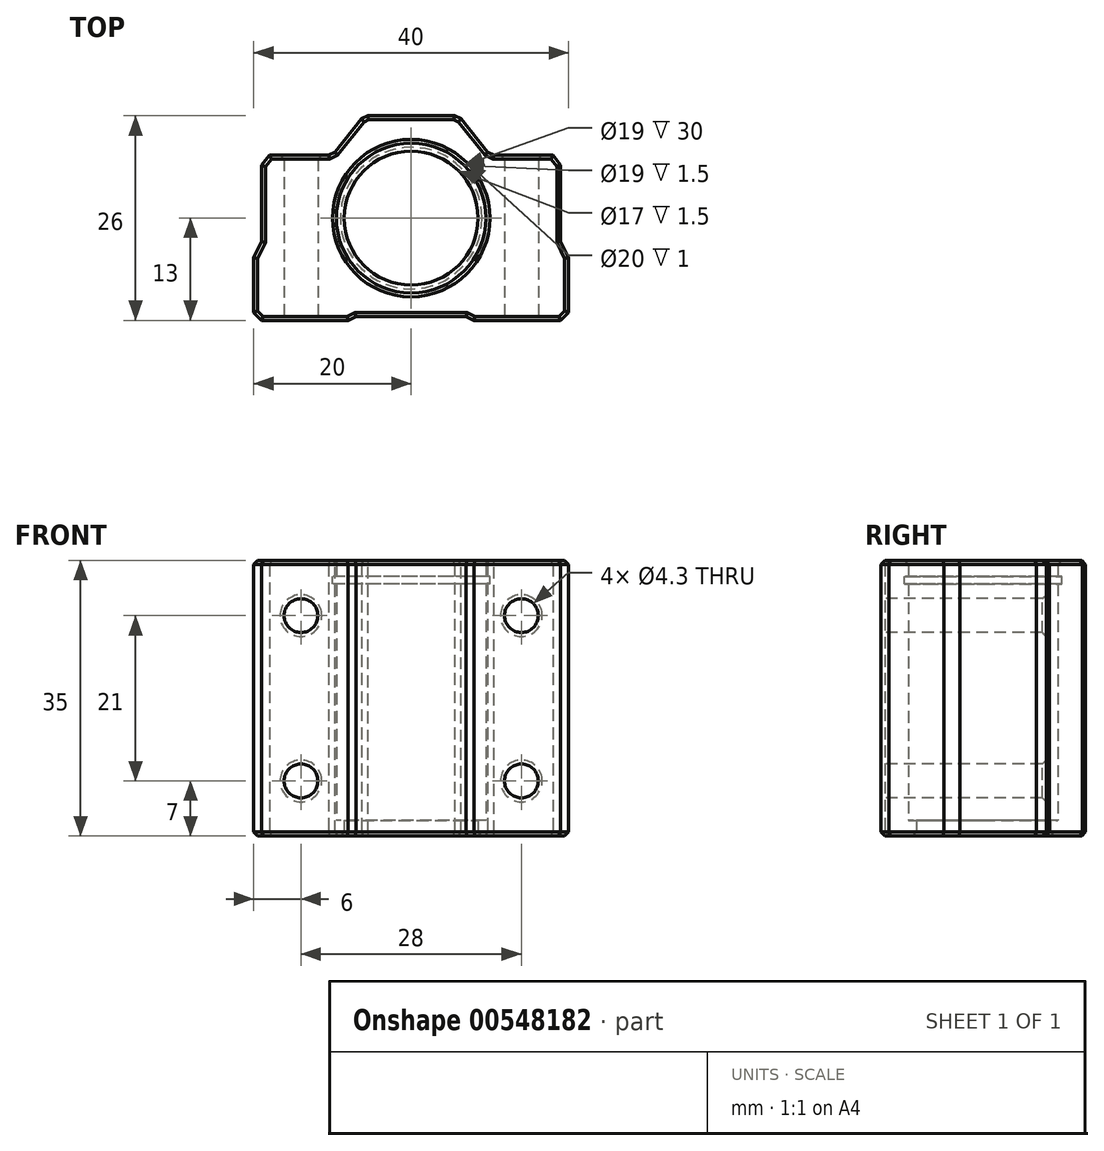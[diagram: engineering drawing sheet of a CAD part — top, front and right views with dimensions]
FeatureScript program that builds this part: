
annotation { "Feature Type Name" : "Feature", "Feature Type Description" : "" }
export const myFeature = defineFeature(function(context is Context, id is Id, definition is map)
    precondition{}
    {
        {
            var Q0;
            Q0=qCreatedBy(makeId("Top.planeOp"),FACE);
            var sketch = newSketch(context, id + "F0", { "sketchPlane" : qUnion([Q0])});
            skLineSegment(sketch, "E0", {"start": v(19, -13) * mm, "end": v(20, -12) * mm});
            skLineSegment(sketch, "E1", {"start": v(20, -12) * mm, "end": v(20, -5) * mm});
            skLineSegment(sketch, "E2", {"start": v(20, -5) * mm, "end": v(19, -3) * mm});
            skLineSegment(sketch, "E3", {"start": v(19, -3) * mm, "end": v(19, 6.72) * mm});
            skLineSegment(sketch, "E4", {"start": v(19, 6.72) * mm, "end": v(18, 8) * mm});
            skLineSegment(sketch, "E5", {"start": v(18, 8) * mm, "end": v(10, 8) * mm});
            skLineSegment(sketch, "E6", {"start": v(10, 8) * mm, "end": v(6, 13) * mm});
            skLineSegment(sketch, "E7", {"start": v(6, 13) * mm, "end": v(-6, 13) * mm});
            skLineSegment(sketch, "E8", {"start": v(-6, 13) * mm, "end": v(-10, 8) * mm});
            skLineSegment(sketch, "E9", {"start": v(-10, 8) * mm, "end": v(-18, 8) * mm});
            skLineSegment(sketch, "E10", {"start": v(-18, 8) * mm, "end": v(-19, 6.72) * mm});
            skLineSegment(sketch, "E11", {"start": v(-19, 6.72) * mm, "end": v(-19, -3) * mm});
            skLineSegment(sketch, "E12", {"start": v(-19, -3) * mm, "end": v(-20, -5) * mm});
            skLineSegment(sketch, "E13", {"start": v(-20, -5) * mm, "end": v(-20, -12) * mm});
            skLineSegment(sketch, "E14", {"start": v(-20, -12) * mm, "end": v(-19, -13) * mm});
            skCircle(sketch, "E15", {"center": v(0, 0) * mm, "radius": 9.5 * mm});
            skLineSegment(sketch, "E16", {"start": v(-19, -13) * mm, "end": v(-8, -13) * mm});
            skLineSegment(sketch, "E17", {"start": v(-8, -13) * mm, "end": v(-7, -12.5) * mm});
            skLineSegment(sketch, "E18", {"start": v(-7, -12.5) * mm, "end": v(7, -12.5) * mm});
            skLineSegment(sketch, "E19", {"start": v(7, -12.5) * mm, "end": v(8, -13) * mm});
            skLineSegment(sketch, "E20", {"start": v(8, -13) * mm, "end": v(19, -13) * mm});
            skSolve(sketch);
        }
        {
            var Q0;
            Q0=qSketchRegion(id+"F0",true);
            extrude(context, id + "F1", {"entities" : qUnion([Q0]), "depth" : 17.5 * mm, "offsetDistance" : 25 * mm, "hasSecondDirection" : true, "secondDirectionOppositeDirection" : true, "secondDirectionDepth" : 17.5 * mm});
        }
        {
            var Q0;
            Q0=makeQuery(id+"F1.opExtrude","SWEPT_FACE",FACE,{"disambiguationData":[OSD([sQuery(id+"F0.wireOp",EDGE,"E16")])]});
            var sketch = newSketch(context, id + "F2", { "sketchPlane" : qUnion([Q0])});
            skCircle(sketch, "E21", {"center": v(-14, 10.5) * mm, "radius": 2.15 * mm});
            skCircle(sketch, "E22", {"center": v(-14, -10.5) * mm, "radius": 2.15 * mm});
            skCircle(sketch, "E23", {"center": v(14, 10.5) * mm, "radius": 2.15 * mm});
            skCircle(sketch, "E24", {"center": v(14, -10.5) * mm, "radius": 2.15 * mm});
            skSolve(sketch);
        }
        {
            var Q0;
            Q0=makeQuery(id+"F2.imprint","IMPRINT",FACE,{"disambiguationData":[TD([[makeQuery(id+"F2.imprint","IMPRINT",EDGE,{"derivedFrom":sQuery(id+"F2.wireOp",EDGE,"E21")}),1.0]])]});
            var Q1;
            Q1=makeQuery(id+"F2.imprint","IMPRINT",FACE,{"disambiguationData":[TD([[makeQuery(id+"F2.imprint","IMPRINT",EDGE,{"derivedFrom":sQuery(id+"F2.wireOp",EDGE,"E23")}),1.0]])]});
            var Q2;
            Q2=makeQuery(id+"F2.imprint","IMPRINT",FACE,{"disambiguationData":[TD([[makeQuery(id+"F2.imprint","IMPRINT",EDGE,{"derivedFrom":sQuery(id+"F2.wireOp",EDGE,"E24")}),1.0]])]});
            var Q3;
            Q3=makeQuery(id+"F2.imprint","IMPRINT",FACE,{"disambiguationData":[TD([[makeQuery(id+"F2.imprint","IMPRINT",EDGE,{"derivedFrom":sQuery(id+"F2.wireOp",EDGE,"E22")}),1.0]])]});
            var Q4;
            Q4=sQuery(id+"F2.wireOp",EDGE,"E22");
            var Q5;
            Q5=sQuery(id+"F2.wireOp",EDGE,"E21");
            var Q6;
            Q6=sQuery(id+"F2.wireOp",EDGE,"E23");
            var Q7;
            Q7=sQuery(id+"F2.wireOp",EDGE,"E24");
            extrude(context, id + "F3", {"entities" : qUnion([Q0, Q1, Q2, Q3]), "operationType" : NewBodyOperationType.REMOVE, "surfaceEntities" : qUnion([Q4, Q5, Q6, Q7]), "oppositeDirection" : true, "depth" : 25 * mm, "offsetDistance" : 25 * mm});
        }
        {
            var Q0;
            Q0=makeQuery(id+"F3.boolean.opBoolean","INTERSECT",EDGE,{"derivedFrom":[makeQuery(id+"F1.opExtrude","SWEPT_FACE",FACE,{"disambiguationData":[OSD([sQuery(id+"F0.wireOp",EDGE,"E9")])]}),makeQuery(id+"F3.opExtrude","SWEPT_FACE",FACE,{"disambiguationData":[OSD([sQuery(id+"F2.wireOp",EDGE,"E21")])]})]});
            var Q1;
            Q1=makeQuery(id+"F3.boolean.opBoolean","INTERSECT",EDGE,{"derivedFrom":[makeQuery(id+"F1.opExtrude","SWEPT_FACE",FACE,{"disambiguationData":[OSD([sQuery(id+"F0.wireOp",EDGE,"E9")])]}),makeQuery(id+"F3.opExtrude","SWEPT_FACE",FACE,{"disambiguationData":[OSD([sQuery(id+"F2.wireOp",EDGE,"E22")])]})]});
            var Q2;
            Q2=makeQuery(id+"F3.boolean.opBoolean","INTERSECT",EDGE,{"derivedFrom":[makeQuery(id+"F1.opExtrude","SWEPT_FACE",FACE,{"disambiguationData":[OSD([sQuery(id+"F0.wireOp",EDGE,"E5")])]}),makeQuery(id+"F3.opExtrude","SWEPT_FACE",FACE,{"disambiguationData":[OSD([sQuery(id+"F2.wireOp",EDGE,"E24")])]})]});
            var Q3;
            Q3=makeQuery(id+"F3.boolean.opBoolean","INTERSECT",EDGE,{"derivedFrom":[makeQuery(id+"F1.opExtrude","SWEPT_FACE",FACE,{"disambiguationData":[OSD([sQuery(id+"F0.wireOp",EDGE,"E5")])]}),makeQuery(id+"F3.opExtrude","SWEPT_FACE",FACE,{"disambiguationData":[OSD([sQuery(id+"F2.wireOp",EDGE,"E23")])]})]});
            var Q4;
            Q4=makeQuery(id+"F3.boolean.opBoolean","COPY",EDGE,{"derivedFrom":makeQuery(id+"F3.opExtrude","CAP_EDGE",EDGE,{"disambiguationData":[OSD([sQuery(id+"F2.wireOp",EDGE,"E21")])],"isStart":true})});
            var Q5;
            Q5=makeQuery(id+"F3.boolean.opBoolean","COPY",EDGE,{"derivedFrom":makeQuery(id+"F3.opExtrude","CAP_EDGE",EDGE,{"disambiguationData":[OSD([sQuery(id+"F2.wireOp",EDGE,"E22")])],"isStart":true})});
            var Q6;
            Q6=makeQuery(id+"F3.boolean.opBoolean","COPY",EDGE,{"derivedFrom":makeQuery(id+"F3.opExtrude","CAP_EDGE",EDGE,{"disambiguationData":[OSD([sQuery(id+"F2.wireOp",EDGE,"E24")])],"isStart":true})});
            var Q7;
            Q7=makeQuery(id+"F3.boolean.opBoolean","COPY",EDGE,{"derivedFrom":makeQuery(id+"F3.opExtrude","CAP_EDGE",EDGE,{"disambiguationData":[OSD([sQuery(id+"F2.wireOp",EDGE,"E23")])],"isStart":true})});
            chamfer(context, id + "F4", {"entities" : qUnion([Q0, Q1, Q2, Q3, Q4, Q5, Q6, Q7]), "width" : .5 * mm, "tangentPropagation" : true});
        }
        {
            var Q0;
            Q0=makeQuery(id+"F1.opExtrude","CAP_FACE",FACE,{"disambiguationData":[OSD([sQuery(id+"F0.wireOp",EDGE,"E0"),sQuery(id+"F0.wireOp",EDGE,"E1"),sQuery(id+"F0.wireOp",EDGE,"E2"),sQuery(id+"F0.wireOp",EDGE,"E3"),sQuery(id+"F0.wireOp",EDGE,"E4"),sQuery(id+"F0.wireOp",EDGE,"E5"),sQuery(id+"F0.wireOp",EDGE,"E6"),sQuery(id+"F0.wireOp",EDGE,"E7"),sQuery(id+"F0.wireOp",EDGE,"E8"),sQuery(id+"F0.wireOp",EDGE,"E9"),sQuery(id+"F0.wireOp",EDGE,"E10"),sQuery(id+"F0.wireOp",EDGE,"E11"),sQuery(id+"F0.wireOp",EDGE,"E12"),sQuery(id+"F0.wireOp",EDGE,"E13"),sQuery(id+"F0.wireOp",EDGE,"E14"),sQuery(id+"F0.wireOp",EDGE,"E15"),sQuery(id+"F0.wireOp",EDGE,"E16"),sQuery(id+"F0.wireOp",EDGE,"E17"),sQuery(id+"F0.wireOp",EDGE,"E18"),sQuery(id+"F0.wireOp",EDGE,"E19"),sQuery(id+"F0.wireOp",EDGE,"E20")])],"isStart":true});
            var sketch = newSketch(context, id + "F5", { "sketchPlane" : qUnion([Q0])});
            skCircle(sketch, "E25", {"center": v(0, 0) * mm, "radius": 8.5 * mm});
            skSolve(sketch);
        }
        {
            var Q0;
            Q0=makeQuery(id+"F5.imprint","IMPRINT",FACE,{"disambiguationData":[TD([[makeQuery(id+"F5.imprint","IMPRINT",EDGE,{"derivedFrom":sQuery(id+"F5.wireOp",EDGE,"E25")}),-1.0]])]});
            extrude(context, id + "F6", {"entities" : qUnion([Q0]), "operationType" : NewBodyOperationType.ADD, "oppositeDirection" : true, "depth" : 2 * mm, "offsetDistance" : 25 * mm});
        }
        {
            var Q0;
            Q0=makeQuery(id+"F1.opExtrude","CAP_FACE",FACE,{"disambiguationData":[OSD([sQuery(id+"F0.wireOp",EDGE,"E0"),sQuery(id+"F0.wireOp",EDGE,"E1"),sQuery(id+"F0.wireOp",EDGE,"E2"),sQuery(id+"F0.wireOp",EDGE,"E3"),sQuery(id+"F0.wireOp",EDGE,"E4"),sQuery(id+"F0.wireOp",EDGE,"E5"),sQuery(id+"F0.wireOp",EDGE,"E6"),sQuery(id+"F0.wireOp",EDGE,"E7"),sQuery(id+"F0.wireOp",EDGE,"E8"),sQuery(id+"F0.wireOp",EDGE,"E9"),sQuery(id+"F0.wireOp",EDGE,"E10"),sQuery(id+"F0.wireOp",EDGE,"E11"),sQuery(id+"F0.wireOp",EDGE,"E12"),sQuery(id+"F0.wireOp",EDGE,"E13"),sQuery(id+"F0.wireOp",EDGE,"E14"),sQuery(id+"F0.wireOp",EDGE,"E15"),sQuery(id+"F0.wireOp",EDGE,"E16"),sQuery(id+"F0.wireOp",EDGE,"E17"),sQuery(id+"F0.wireOp",EDGE,"E18"),sQuery(id+"F0.wireOp",EDGE,"E19"),sQuery(id+"F0.wireOp",EDGE,"E20")])],"isStart":false});
            cPlane(context, id + "F7", {"entities" : qUnion([Q0]), "cplaneType" : CPlaneType.OFFSET, "offset" : 2 * mm, "oppositeDirection" : true, "width" : 150 * mm, "height" : 150 * mm});
        }
        {
            var Q0;
            Q0=qCreatedBy(id+"F7.planeOp",FACE);
            var sketch = newSketch(context, id + "F8", { "sketchPlane" : qUnion([Q0])});
            skCircle(sketch, "E26", {"center": v(0, 0) * mm, "radius": 10 * mm});
            skSolve(sketch);
        }
        {
            var Q0;
            Q0=qSketchRegion(id+"F8",true);
            extrude(context, id + "F9", {"entities" : qUnion([Q0]), "operationType" : NewBodyOperationType.REMOVE, "oppositeDirection" : true, "depth" : 1 * mm, "offsetDistance" : 25 * mm});
        }
        {
            var Q0;
            Q0=makeQuery(id+"F1.opExtrude","SWEPT_EDGE",EDGE,{"disambiguationData":[OSD([sQuery(id+"F0.wireOp",EDGE,"E8"),sQuery(id+"F0.wireOp",EDGE,"E9")])]});
            var Q1;
            Q1=makeQuery(id+"F1.opExtrude","SWEPT_EDGE",EDGE,{"disambiguationData":[OSD([sQuery(id+"F0.wireOp",EDGE,"E7"),sQuery(id+"F0.wireOp",EDGE,"E8")])]});
            var Q2;
            Q2=makeQuery(id+"F1.opExtrude","SWEPT_EDGE",EDGE,{"disambiguationData":[OSD([sQuery(id+"F0.wireOp",EDGE,"E6"),sQuery(id+"F0.wireOp",EDGE,"E7")])]});
            var Q3;
            Q3=makeQuery(id+"F1.opExtrude","SWEPT_EDGE",EDGE,{"disambiguationData":[OSD([sQuery(id+"F0.wireOp",EDGE,"E5"),sQuery(id+"F0.wireOp",EDGE,"E6")])]});
            chamfer(context, id + "F10", {"entities" : qUnion([Q0, Q1, Q2, Q3]), "width" : .5 * mm, "tangentPropagation" : true});
        }
        {
            var Q0;
            Q0=makeQuery(id+"F1.opExtrude","CAP_FACE",FACE,{"disambiguationData":[OSD([sQuery(id+"F0.wireOp",EDGE,"E0"),sQuery(id+"F0.wireOp",EDGE,"E1"),sQuery(id+"F0.wireOp",EDGE,"E2"),sQuery(id+"F0.wireOp",EDGE,"E3"),sQuery(id+"F0.wireOp",EDGE,"E4"),sQuery(id+"F0.wireOp",EDGE,"E5"),sQuery(id+"F0.wireOp",EDGE,"E6"),sQuery(id+"F0.wireOp",EDGE,"E7"),sQuery(id+"F0.wireOp",EDGE,"E8"),sQuery(id+"F0.wireOp",EDGE,"E9"),sQuery(id+"F0.wireOp",EDGE,"E10"),sQuery(id+"F0.wireOp",EDGE,"E11"),sQuery(id+"F0.wireOp",EDGE,"E12"),sQuery(id+"F0.wireOp",EDGE,"E13"),sQuery(id+"F0.wireOp",EDGE,"E14"),sQuery(id+"F0.wireOp",EDGE,"E15"),sQuery(id+"F0.wireOp",EDGE,"E16"),sQuery(id+"F0.wireOp",EDGE,"E17"),sQuery(id+"F0.wireOp",EDGE,"E18"),sQuery(id+"F0.wireOp",EDGE,"E19"),sQuery(id+"F0.wireOp",EDGE,"E20")])],"isStart":false});
            chamfer(context, id + "F11", {"entities" : qUnion([Q0]), "width" : .5 * mm, "tangentPropagation" : true});
        }
        {
            var Q0;
            {var subQ0=sQuery(id+"F0.wireOp",EDGE,"E15");Q0=makeQuery(id+"F6.boolean.opBoolean","MERGE",FACE,{"derivedFrom":[makeQuery(id+"F1.opExtrude","CAP_FACE",FACE,{"disambiguationData":[OSD([sQuery(id+"F0.wireOp",EDGE,"E0"),sQuery(id+"F0.wireOp",EDGE,"E1"),sQuery(id+"F0.wireOp",EDGE,"E2"),sQuery(id+"F0.wireOp",EDGE,"E3"),sQuery(id+"F0.wireOp",EDGE,"E4"),sQuery(id+"F0.wireOp",EDGE,"E5"),sQuery(id+"F0.wireOp",EDGE,"E6"),sQuery(id+"F0.wireOp",EDGE,"E7"),sQuery(id+"F0.wireOp",EDGE,"E8"),sQuery(id+"F0.wireOp",EDGE,"E9"),sQuery(id+"F0.wireOp",EDGE,"E10"),sQuery(id+"F0.wireOp",EDGE,"E11"),sQuery(id+"F0.wireOp",EDGE,"E12"),sQuery(id+"F0.wireOp",EDGE,"E13"),sQuery(id+"F0.wireOp",EDGE,"E14"),subQ0,sQuery(id+"F0.wireOp",EDGE,"E16"),sQuery(id+"F0.wireOp",EDGE,"E17"),sQuery(id+"F0.wireOp",EDGE,"E18"),sQuery(id+"F0.wireOp",EDGE,"E19"),sQuery(id+"F0.wireOp",EDGE,"E20")])],"isStart":true}),makeQuery(id+"F6.opExtrude","CAP_FACE",FACE,{"disambiguationData":[OSD([subQ0,sQuery(id+"F5.wireOp",EDGE,"E25")])],"isStart":true})]});}
            chamfer(context, id + "F12", {"entities" : qUnion([Q0]), "width" : .5 * mm, "tangentPropagation" : true});
        }
    });
